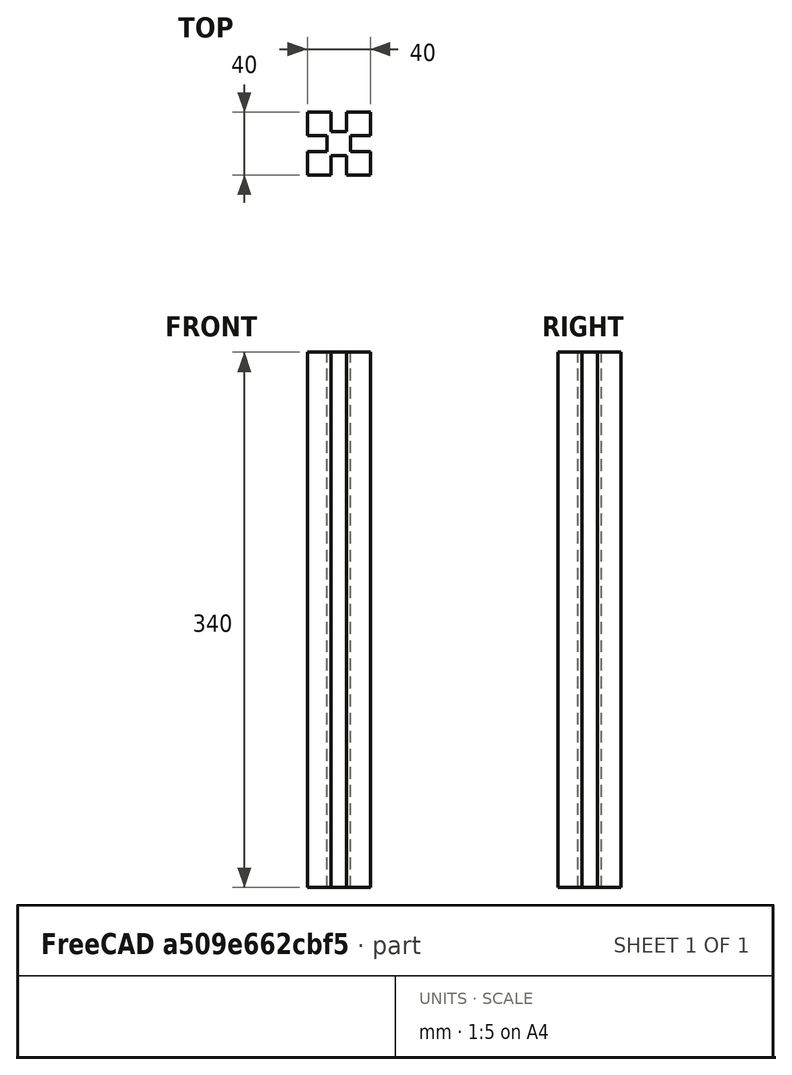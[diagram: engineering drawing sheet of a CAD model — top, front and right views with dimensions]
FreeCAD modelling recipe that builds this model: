
FCSTD DOCUMENT  (FreeCAD 0.18R14555 (Git shallow))
Label: t-slot-profile-340
License: All rights reserved
LicenseURL: http://en.wikipedia.org/wiki/All_rights_reserved
objects: Sketcher::SketchObject×1, PartDesign::Pad×1, PartDesign::Body×1
note: 4 computed .brp shape members not serialized (recipe doc carries the construction recipe); baked Part::Feature solids carry a one-line shape summary decoded from their .brp

FEATURE [Sketcher::SketchObject] Sketch
  MapMode = 5
  Support = -> [XY_Plane]
  sketch-geometry (30):
    g0: LineSegment StartX=-20 StartY=-20 StartZ=0 EndX=-20 EndY=-5 EndZ=0
    g1: LineSegment StartX=-20 StartY=-5 StartZ=0 EndX=-7.5 EndY=-5 EndZ=0
    g2: LineSegment StartX=-7.5 StartY=-5 StartZ=0 EndX=-7.5 EndY=5 EndZ=0
    g3: LineSegment StartX=-7.5 StartY=5 StartZ=0 EndX=-20 EndY=5 EndZ=0
    g4: LineSegment StartX=-20 StartY=5 StartZ=0 EndX=-20 EndY=20 EndZ=0
    g5: LineSegment StartX=-20 StartY=20 StartZ=0 EndX=-5 EndY=20 EndZ=0
    g6: LineSegment StartX=-5 StartY=20 StartZ=0 EndX=-5 EndY=7.5 EndZ=0
    g7: LineSegment StartX=-5 StartY=7.5 StartZ=0 EndX=5 EndY=7.5 EndZ=0
    g8: LineSegment StartX=5 StartY=7.5 StartZ=0 EndX=5 EndY=20 EndZ=0
    g9: LineSegment StartX=5 StartY=20 StartZ=0 EndX=20 EndY=20 EndZ=0
    g10: LineSegment StartX=20 StartY=20 StartZ=0 EndX=20 EndY=5 EndZ=0
    g11: LineSegment StartX=20 StartY=5 StartZ=0 EndX=7.5 EndY=5 EndZ=0
    g12: LineSegment StartX=7.5 StartY=5 StartZ=0 EndX=7.5 EndY=-5 EndZ=0
    g13: LineSegment StartX=7.5 StartY=-5 StartZ=0 EndX=20 EndY=-5 EndZ=0
    g14: LineSegment StartX=20 StartY=-5 StartZ=0 EndX=20 EndY=-20 EndZ=0
    g15: LineSegment StartX=20 StartY=-20 StartZ=0 EndX=5 EndY=-20 EndZ=0
    g16: LineSegment StartX=5 StartY=-20 StartZ=0 EndX=5 EndY=-7.5 EndZ=0
    g17: LineSegment StartX=5 StartY=-7.5 StartZ=0 EndX=-5 EndY=-7.5 EndZ=0
    g18: LineSegment StartX=-5 StartY=-7.5 StartZ=0 EndX=-5 EndY=-20 EndZ=0
    g19: LineSegment StartX=-5 StartY=-20 StartZ=0 EndX=-20 EndY=-20 EndZ=0
    g20: LineSegment [constr] StartX=-5 StartY=-7.5 StartZ=0 EndX=-5 EndY=7.5 EndZ=0
    g21: LineSegment [constr] StartX=5 StartY=7.5 StartZ=0 EndX=5 EndY=-7.5 EndZ=0
    g22: LineSegment [constr] StartX=-7.5 StartY=5 StartZ=0 EndX=7.5 EndY=5 EndZ=0
    g23: LineSegment [constr] StartX=7.5 StartY=-5 StartZ=0 EndX=-7.5 EndY=-5 EndZ=0
    g24: LineSegment [constr] StartX=-20 StartY=-5 StartZ=0 EndX=-20 EndY=5 EndZ=0
    g25: LineSegment [constr] StartX=-5 StartY=20 StartZ=0 EndX=5 EndY=20 EndZ=0
    g26: LineSegment [constr] StartX=20 StartY=5 StartZ=0 EndX=20 EndY=-5 EndZ=0
    g27: LineSegment [constr] StartX=-5 StartY=-20 StartZ=0 EndX=5 EndY=-20 EndZ=0
    g28: LineSegment [constr] StartX=20 StartY=-20 StartZ=0 EndX=-20 EndY=20 EndZ=0
    g29: LineSegment [constr] StartX=-20 StartY=-20 StartZ=0 EndX=20 EndY=20 EndZ=0
  constraints (80):
    c: Vertical(g0)
    c: Coincident(g0,g1)
    c: Horizontal(g1)
    c: Coincident(g1,g2)
    c: Vertical(g2)
    c: Coincident(g2,g3)
    c: Horizontal(g3)
    c: Coincident(g3,g4)
    c: Vertical(g4)
    c: Coincident(g4,g5)
    c: Horizontal(g5)
    c: Coincident(g5,g6)
    c: Vertical(g6)
    c: Coincident(g6,g7)
    c: Horizontal(g7)
    c: Coincident(g7,g8)
    c: Vertical(g8)
    c: Coincident(g8,g9)
    c: Horizontal(g9)
    c: Coincident(g9,g10)
    c: Vertical(g10)
    c: Coincident(g10,g11)
    c: Coincident(g11,g12)
    c: Coincident(g12,g13)
    c: Horizontal(g13)
    c: Coincident(g13,g14)
    c: Vertical(g14)
    c: Coincident(g14,g15)
    c: Horizontal(g15)
    c: Coincident(g15,g16)
    c: Vertical(g16)
    c: Coincident(g16,g17)
    c: Horizontal(g17)
    c: Coincident(g17,g18)
    c: Vertical(g18)
    c: Coincident(g18,g19)
    c: Coincident(g19,g0)
    c: Horizontal(g19)
    c: Horizontal(g11)
    c: Vertical(g12)
    c: Coincident(g20,g17)
    c: Coincident(g20,g6)
    c: Coincident(g21,g7)
    c: Coincident(g21,g16)
    c: Vertical(g21)
    c: Vertical(g20)
    c: Coincident(g22,g2)
    c: Coincident(g22,g11)
    c: Coincident(g23,g12)
    c: Coincident(g23,g1)
    c: Horizontal(g23)
    c: Horizontal(g22)
    c: Coincident(g24,g0)
    c: Coincident(g24,g3)
    c: Vertical(g24)
    c: Coincident(g25,g5)
    c: Coincident(g25,g8)
    c: Horizontal(g25)
    c: Coincident(g26,g10)
    c: Coincident(g26,g13)
    c: Vertical(g26)
    c: Coincident(g27,g18)
    c: Coincident(g27,g15)
    c: Horizontal(g27)
    c: Coincident(g28,g14)
    c: Coincident(g29,g0)
    c: Coincident(g29,g9)
    c: Coincident(g28,g4)
    c: Equal(g0,g19)
    c: Equal(g4,g5)
    c: Equal(g9,g10)
    c: Equal(g2,g7)
    c: Equal(g3,g6)
    c: Equal(g11,g3)
    c: Equal(g1,g18)
    c: DistanceY(g0,g4) = 40
    c: DistanceY(g2,g2) = 10
    c: DistanceY(g18,g18) = 12.5
    c: PointOnObject(g-1,g29)
    c: PointOnObject(g-1,g28)
FEATURE [PartDesign::Pad] Pad
  Length = 340
  Length2 = 100
  Profile = -> Sketch
  Type = 0
FEATURE [PartDesign::Body] Body
  Group = -> [Sketch,Pad]
  Origin = -> Origin
  Tip = -> Pad
